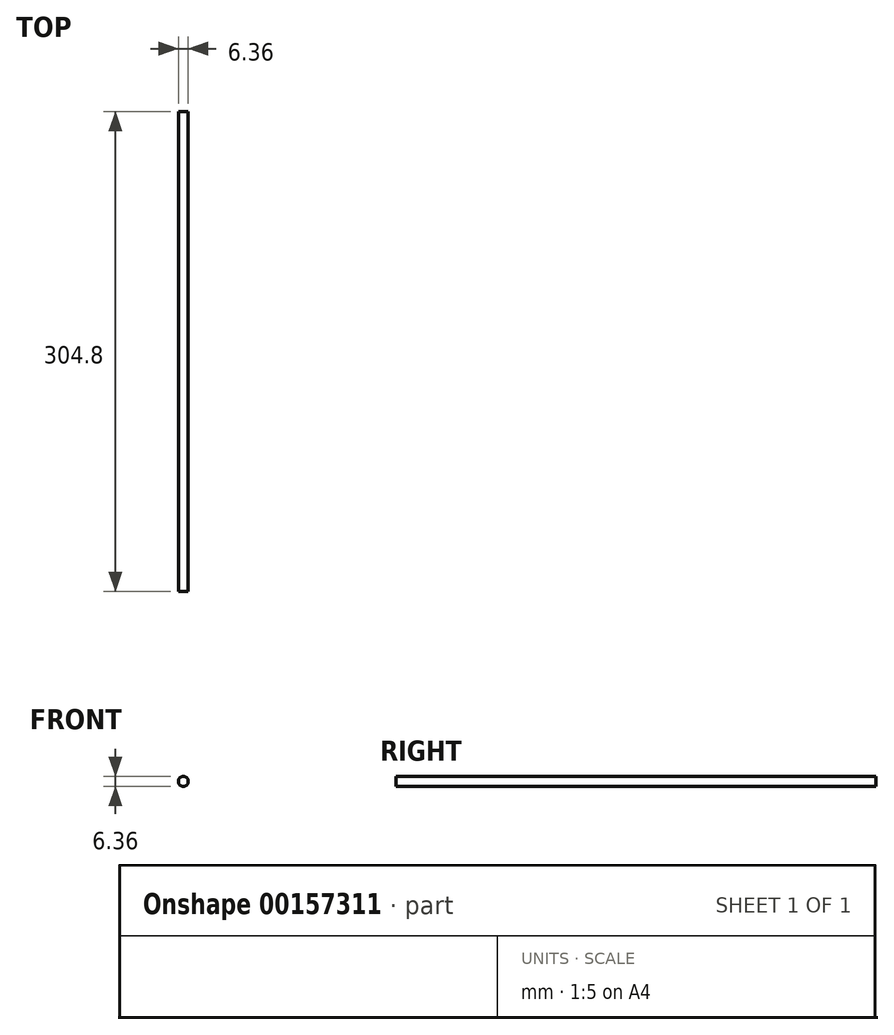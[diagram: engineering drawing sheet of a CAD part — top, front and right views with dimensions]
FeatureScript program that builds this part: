
annotation { "Feature Type Name" : "Feature", "Feature Type Description" : "" }
export const myFeature = defineFeature(function(context is Context, id is Id, definition is map)
    precondition{}
    {
        {
            var Q0;
            Q0=qCreatedBy(makeId("Front.planeOp"),FACE);
            var sketch = newSketch(context, id + "F0", { "sketchPlane" : qUnion([Q0])});
            skCircle(sketch, "E0", {"center": v(0, 0) * mm, "radius": 3.18 * mm});
            skSolve(sketch);
        }
        {
            var Q0;
            Q0 = qSketchRegion(id + "F0", true);
            extrude(context, id + "F1", {"entities" : qUnion([Q0]), "depth" : 304.8 * mm});
        }
    });
